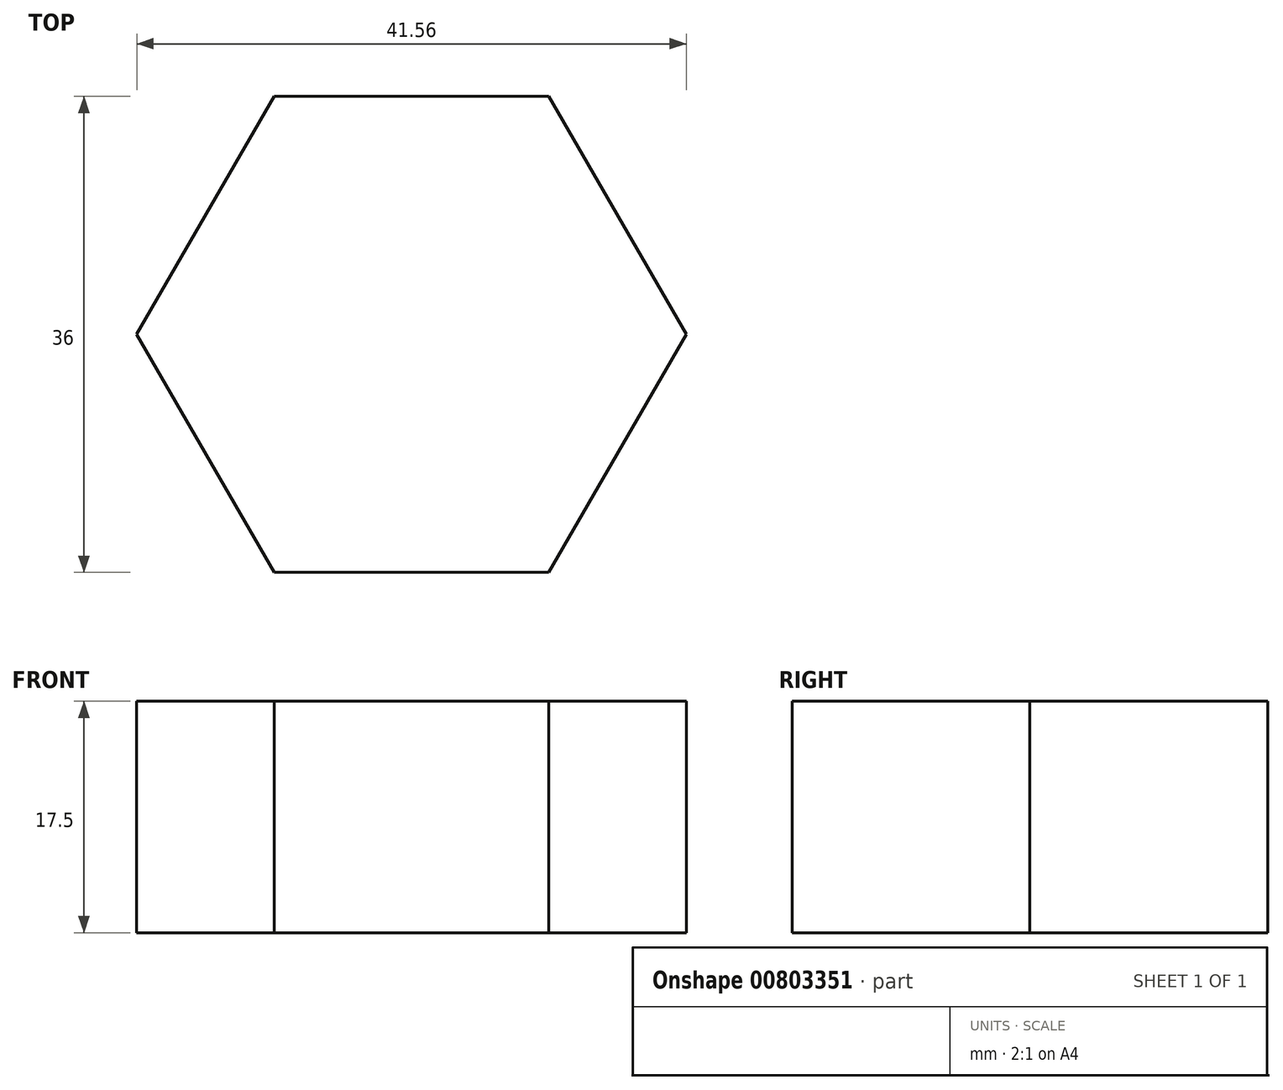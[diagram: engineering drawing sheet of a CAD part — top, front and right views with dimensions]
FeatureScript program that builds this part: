
annotation { "Feature Type Name" : "Feature", "Feature Type Description" : "" }
export const myFeature = defineFeature(function(context is Context, id is Id, definition is map)
    precondition{}
    {
        {
            var Q0;
            Q0=qCreatedBy(makeId("Top.planeOp"),FACE);
            var sketch = newSketch(context, id + "F0", { "sketchPlane" : qUnion([Q0])});
            skCircle(sketch, "E0.cCircle", {"center": v(0, 0) * mm, "radius": 18 * mm, "construction": true});
            skLineSegment(sketch, "E0.0", {"start": v(-20.78, 0) * mm, "end": v(-10.4, 18) * mm});
            skLineSegment(sketch, "E0.1", {"start": v(-10.4, 18) * mm, "end": v(10.4, 18) * mm});
            skLineSegment(sketch, "E0.2", {"start": v(10.4, 18) * mm, "end": v(20.78, 0) * mm});
            skLineSegment(sketch, "E0.3", {"start": v(20.78, 0) * mm, "end": v(10.4, -18) * mm});
            skLineSegment(sketch, "E0.4", {"start": v(10.4, -18) * mm, "end": v(-10.4, -18) * mm});
            skLineSegment(sketch, "E0.5", {"start": v(-10.4, -18) * mm, "end": v(-20.78, 0) * mm});
            skPoint(sketch, "E0.0.midPoint", {"position": v(-15.59, 9) * mm});
            skSolve(sketch);
        }
        {
            var Q0;
            Q0 = qSketchRegion(id + "F0", true);
            extrude(context, id + "F1", {"entities" : qUnion([Q0]), "depth" : 17.5 * mm, "offsetDistance" : 25 * mm});
        }
    });
